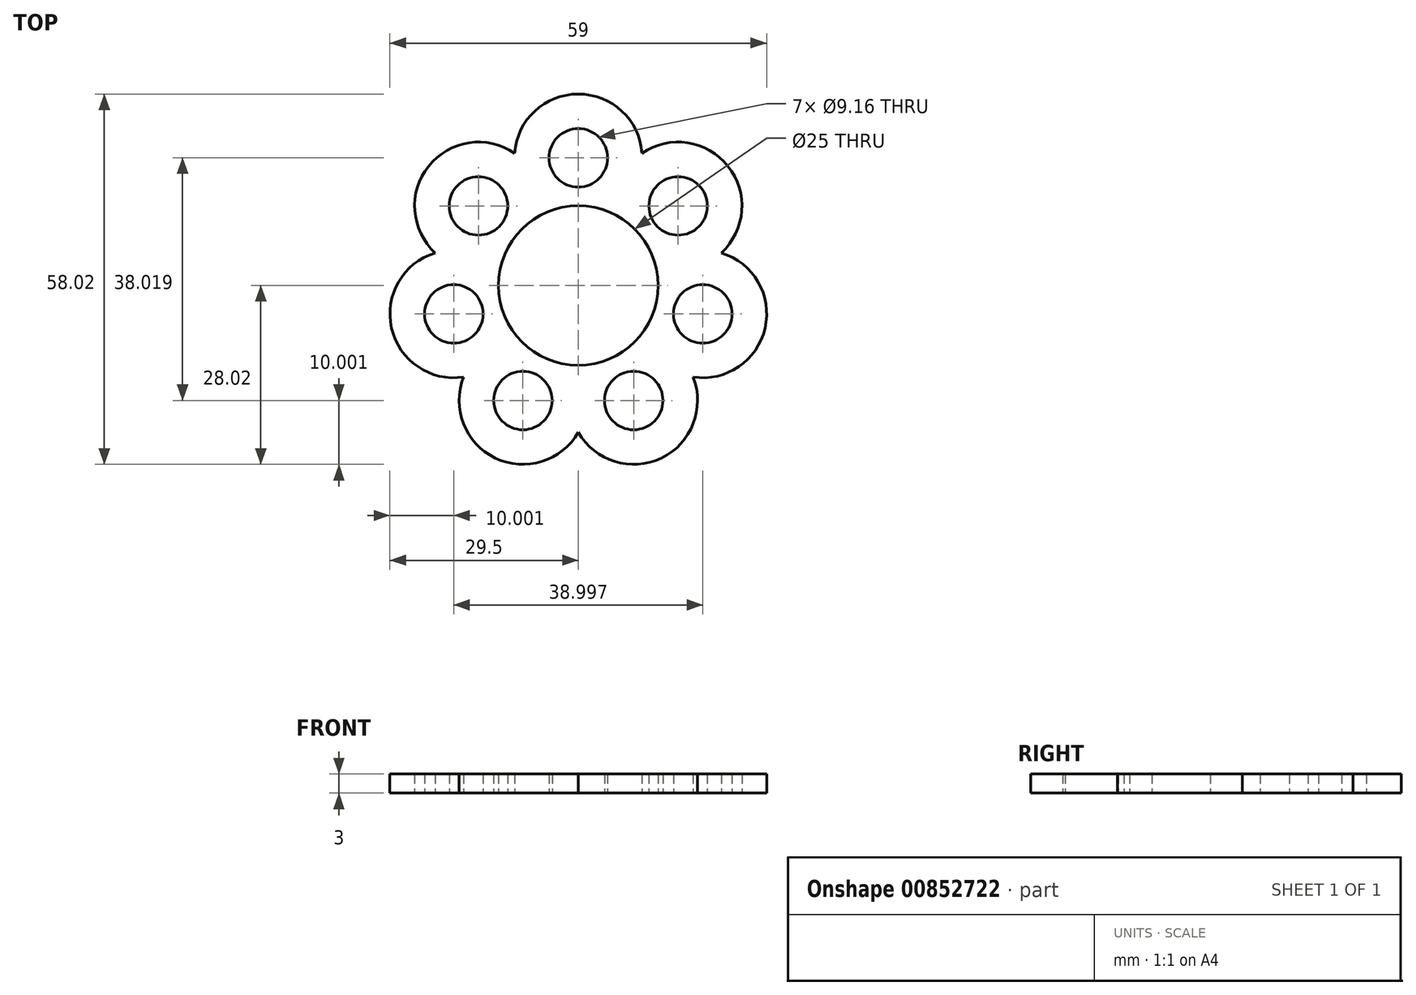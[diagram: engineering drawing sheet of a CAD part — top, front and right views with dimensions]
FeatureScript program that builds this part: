
annotation { "Feature Type Name" : "Feature", "Feature Type Description" : "" }
export const myFeature = defineFeature(function(context is Context, id is Id, definition is map)
    precondition{}
    {
        {
            var Q0;
            Q0=qCreatedBy(makeId("Top.planeOp"),FACE);
            var sketch = newSketch(context, id + "F0", { "sketchPlane" : qUnion([Q0])});
            skCircle(sketch, "E0", {"center": v(0, 0) * mm, "radius": 8 * mm});
            skCircle(sketch, "E1", {"center": v(0, 20) * mm, "radius": 4.58 * mm});
            skArc(sketch, "E2", {"start": v(9.97, 20.71) * mm, "mid": v(0, 30) * mm, "end": v(-9.97, 20.71) * mm});
            skCircle(sketch, "E3.1.0", {"center": v(-15.64, 12.47) * mm, "radius": 4.58 * mm});
            skArc(sketch, "E3.1.1", {"start": v(-9.97, 20.71) * mm, "mid": v(-23.45, 18.7) * mm, "end": v(-22.41, 5.12) * mm});
            skCircle(sketch, "E3.2.0", {"center": v(-19.5, -4.45) * mm, "radius": 4.58 * mm});
            skArc(sketch, "E3.2.1", {"start": v(-22.41, 5.12) * mm, "mid": v(-29.25, -6.68) * mm, "end": v(-17.97, -14.33) * mm});
            skCircle(sketch, "E3.3.0", {"center": v(-8.68, -18.02) * mm, "radius": 4.58 * mm});
            skArc(sketch, "E3.3.1", {"start": v(-17.97, -14.33) * mm, "mid": v(-13.02, -27.03) * mm, "end": v(0, -22.99) * mm});
            skCircle(sketch, "E3.4.0", {"center": v(8.68, -18.02) * mm, "radius": 4.58 * mm});
            skArc(sketch, "E3.4.1", {"start": v(0, -22.99) * mm, "mid": v(13.02, -27.03) * mm, "end": v(17.97, -14.33) * mm});
            skCircle(sketch, "E3.5.0", {"center": v(19.5, -4.45) * mm, "radius": 4.58 * mm});
            skCircle(sketch, "E3.6.0", {"center": v(15.64, 12.47) * mm, "radius": 4.58 * mm});
            skArc(sketch, "E4.trimOffspring", {"start": v(22.41, 5.12) * mm, "mid": v(23.45, 18.7) * mm, "end": v(9.97, 20.71) * mm});
            skArc(sketch, "E5.trimOffspring", {"start": v(17.97, -14.33) * mm, "mid": v(29.25, -6.68) * mm, "end": v(22.41, 5.12) * mm});
            skCircle(sketch, "E6", {"center": v(0, 0) * mm, "radius": 12.5 * mm});
            skSolve(sketch);
        }
        {
            var Q0;
            Q0 = qSketchRegion(id + "F0", true);
            extrude(context, id + "F1", {"entities" : qUnion([Q0]), "depth" : 3 * mm, "offsetDistance" : 25 * mm});
        }
    });
